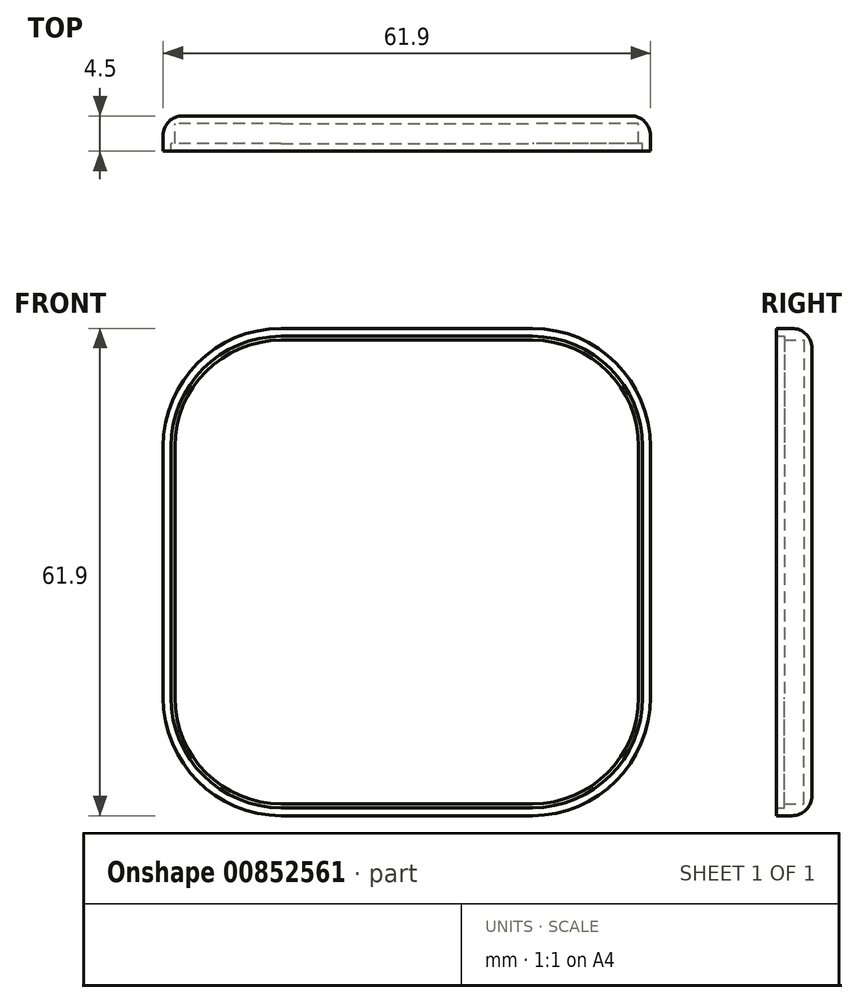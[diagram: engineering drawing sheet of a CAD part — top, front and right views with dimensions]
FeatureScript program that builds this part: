
annotation { "Feature Type Name" : "Feature", "Feature Type Description" : "" }
export const myFeature = defineFeature(function(context is Context, id is Id, definition is map)
    precondition{}
    {
        {
            var Q0;
            Q0=qCreatedBy(makeId("Front.planeOp"),FACE);
            var sketch = newSketch(context, id + "F0", { "sketchPlane" : qUnion([Q0])});
            skLineSegment(sketch, "E0.bottom", {"start": v(-15.95, 30.95) * mm, "end": v(15.95, 30.95) * mm});
            skLineSegment(sketch, "E0.top", {"start": v(-15.95, -30.95) * mm, "end": v(15.95, -30.95) * mm});
            skLineSegment(sketch, "E0.left", {"start": v(-30.95, 15.95) * mm, "end": v(-30.95, -15.95) * mm});
            skLineSegment(sketch, "E0.right", {"start": v(30.95, 15.95) * mm, "end": v(30.95, -15.95) * mm});
            skLineSegment(sketch, "E1", {"start": v(-30.95, 30.95) * mm, "end": v(30.95, -30.95) * mm, "construction": true});
            skLineSegment(sketch, "E2", {"start": v(30.95, 30.95) * mm, "end": v(-30.95, -30.95) * mm, "construction": true});
            skPoint(sketch, "E3.visualSharp", {"position": v(-30.95, 30.95) * mm});
            skArc(sketch, "E3.filletArc", {"start": v(-15.95, 30.95) * mm, "mid": v(-26.56, 26.56) * mm, "end": v(-30.95, 15.95) * mm});
            skPoint(sketch, "E4.visualSharp", {"position": v(30.95, 30.95) * mm});
            skArc(sketch, "E4.filletArc", {"start": v(30.95, 15.95) * mm, "mid": v(26.56, 26.56) * mm, "end": v(15.95, 30.95) * mm});
            skPoint(sketch, "E5.visualSharp", {"position": v(30.95, -30.95) * mm});
            skArc(sketch, "E5.filletArc", {"start": v(15.95, -30.95) * mm, "mid": v(26.56, -26.56) * mm, "end": v(30.95, -15.95) * mm});
            skPoint(sketch, "E6.visualSharp", {"position": v(-30.95, -30.95) * mm});
            skArc(sketch, "E6.filletArc", {"start": v(-30.95, -15.95) * mm, "mid": v(-26.56, -26.56) * mm, "end": v(-15.95, -30.95) * mm});
            skArc(sketch, "E7.0", {"start": v(-15.95, 29.45) * mm, "mid": v(-25.5, 25.5) * mm, "end": v(-29.45, 15.95) * mm});
            skLineSegment(sketch, "E7.1", {"start": v(-29.45, 15.95) * mm, "end": v(-29.45, -15.95) * mm});
            skLineSegment(sketch, "E7.2", {"start": v(-15.95, 29.45) * mm, "end": v(15.95, 29.45) * mm});
            skArc(sketch, "E7.3", {"start": v(-29.45, -15.95) * mm, "mid": v(-25.5, -25.5) * mm, "end": v(-15.95, -29.45) * mm});
            skArc(sketch, "E7.4", {"start": v(29.45, 15.95) * mm, "mid": v(25.5, 25.5) * mm, "end": v(15.95, 29.45) * mm});
            skLineSegment(sketch, "E7.5", {"start": v(29.45, 15.95) * mm, "end": v(29.45, -15.95) * mm});
            skArc(sketch, "E7.6", {"start": v(15.95, -29.45) * mm, "mid": v(25.5, -25.5) * mm, "end": v(29.45, -15.95) * mm});
            skLineSegment(sketch, "E7.7", {"start": v(-15.95, -29.45) * mm, "end": v(15.95, -29.45) * mm});
            skArc(sketch, "E8.0", {"start": v(-15.95, 29.95) * mm, "mid": v(-25.85, 25.85) * mm, "end": v(-29.95, 15.95) * mm});
            skLineSegment(sketch, "E8.1", {"start": v(-29.95, 15.95) * mm, "end": v(-29.95, -15.95) * mm});
            skLineSegment(sketch, "E8.2", {"start": v(-15.95, 29.95) * mm, "end": v(15.95, 29.95) * mm});
            skArc(sketch, "E8.3", {"start": v(-29.95, -15.95) * mm, "mid": v(-25.85, -25.85) * mm, "end": v(-15.95, -29.95) * mm});
            skArc(sketch, "E8.4", {"start": v(29.95, 15.95) * mm, "mid": v(25.85, 25.85) * mm, "end": v(15.95, 29.95) * mm});
            skLineSegment(sketch, "E8.5", {"start": v(29.95, 15.95) * mm, "end": v(29.95, -15.95) * mm});
            skArc(sketch, "E8.6", {"start": v(15.95, -29.95) * mm, "mid": v(25.85, -25.85) * mm, "end": v(29.95, -15.95) * mm});
            skLineSegment(sketch, "E8.7", {"start": v(-15.95, -29.95) * mm, "end": v(15.95, -29.95) * mm});
            skSolve(sketch);
        }
        {
            var Q0;
            Q0=makeQuery(id+"F0.imprint","IMPRINT",FACE,{"disambiguationData":[TD([[makeQuery(id+"F0.imprint","IMPRINT",EDGE,{"derivedFrom":sQuery(id+"F0.wireOp",EDGE,"E0.bottom")}),-1.0]])]});
            extrude(context, id + "F1", {"entities" : qUnion([Q0]), "depth" : 4.5 * mm, "offsetDistance" : 25 * mm});
        }
        {
            var Q0;
            Q0=makeQuery(id+"F0.imprint","IMPRINT",FACE,{"disambiguationData":[TD([[makeQuery(id+"F0.imprint","IMPRINT",EDGE,{"derivedFrom":sQuery(id+"F0.wireOp",EDGE,"E7.0")}),-1.0]])]});
            extrude(context, id + "F2", {"entities" : qUnion([Q0]), "operationType" : NewBodyOperationType.ADD, "depth" : 3.5 * mm, "offsetDistance" : 25 * mm});
        }
        {
            var Q0;
            Q0=makeQuery(id+"F0.imprint","IMPRINT",FACE,{"disambiguationData":[TD([[makeQuery(id+"F0.imprint","IMPRINT",EDGE,{"derivedFrom":sQuery(id+"F0.wireOp",EDGE,"E7.0")}),1.0]])]});
            extrude(context, id + "F3", {"entities" : qUnion([Q0]), "operationType" : NewBodyOperationType.ADD, "depth" : 1 * mm, "offsetDistance" : 25 * mm});
        }
        {
            var Q0;
            Q0=makeQuery(id+"F1.opExtrude","CAP_EDGE",EDGE,{"disambiguationData":[OSD([sQuery(id+"F0.wireOp",EDGE,"E0.right")])],"isStart":true});
            fillet(context, id + "F4", {"entities" : qUnion([Q0]), "radius" : 2.5 * mm, "tangentPropagation" : true, "allowEdgeOverflow" : false});
        }
    });
